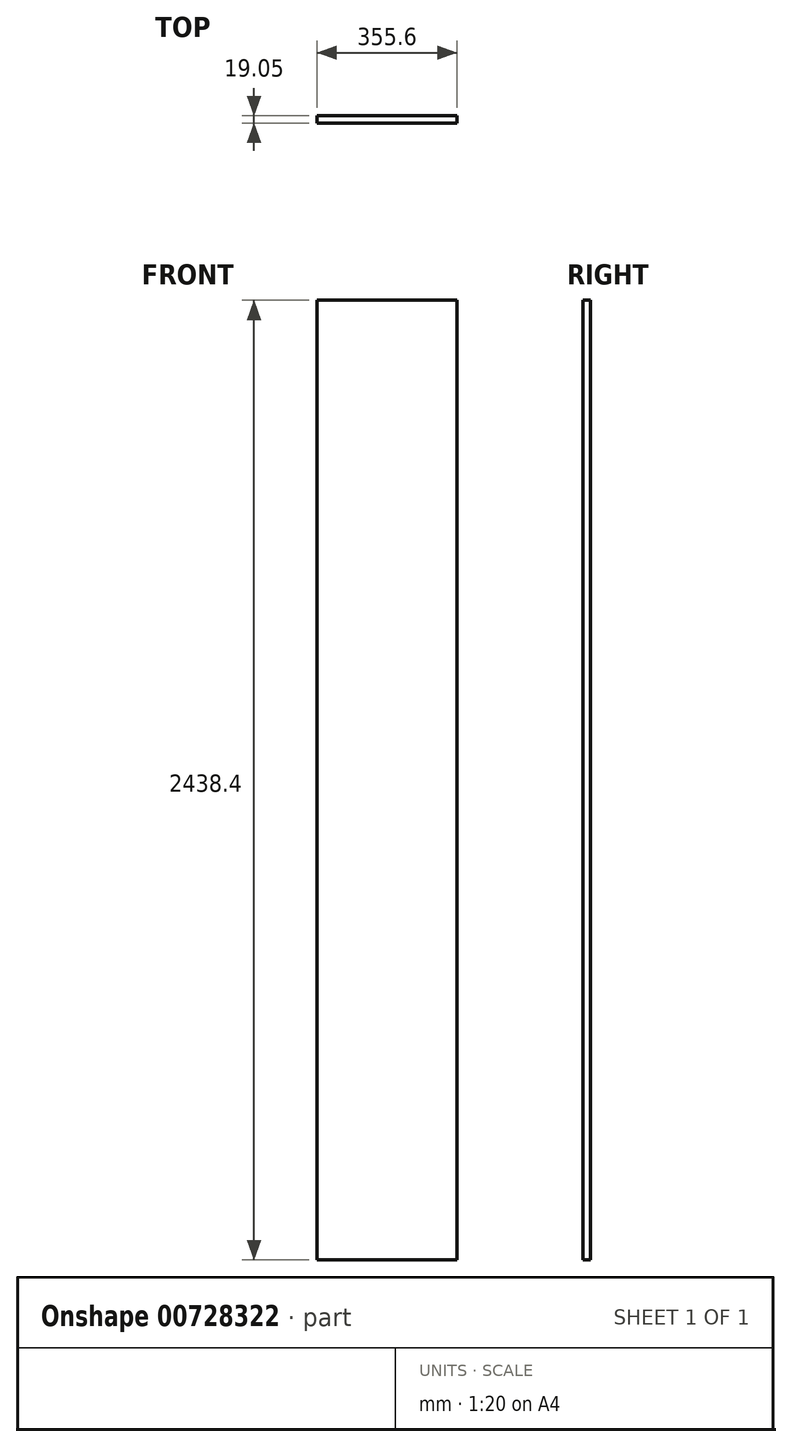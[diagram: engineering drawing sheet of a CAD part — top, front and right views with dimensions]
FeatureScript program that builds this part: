
annotation { "Feature Type Name" : "Feature", "Feature Type Description" : "" }
export const myFeature = defineFeature(function(context is Context, id is Id, definition is map)
    precondition{}
    {
        {
            var Q0;
            Q0=qCreatedBy(makeId("Front.planeOp"),FACE);
            var sketch = newSketch(context, id + "F0", { "sketchPlane" : qUnion([Q0])});
            skLineSegment(sketch, "E0.bottom", {"start": v(177.8, -1219.2) * mm, "end": v(-177.8, -1219.2) * mm});
            skLineSegment(sketch, "E0.top", {"start": v(177.8, 1219.2) * mm, "end": v(-177.8, 1219.2) * mm});
            skLineSegment(sketch, "E0.left", {"start": v(177.8, -1219.2) * mm, "end": v(177.8, 1219.2) * mm});
            skLineSegment(sketch, "E0.right", {"start": v(-177.8, -1219.2) * mm, "end": v(-177.8, 1219.2) * mm});
            skPoint(sketch, "E0.middle", {"position": v(0, 0) * mm});
            skSolve(sketch);
        }
        {
            var Q0;
            Q0=qSketchRegion(id+"F0",true);
            extrude(context, id + "F1", {"entities" : qUnion([Q0]), "depth" : 19.05 * mm});
        }
    });
